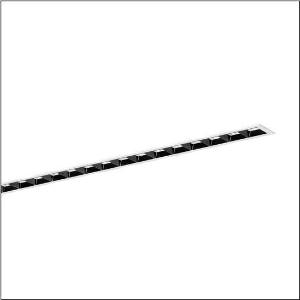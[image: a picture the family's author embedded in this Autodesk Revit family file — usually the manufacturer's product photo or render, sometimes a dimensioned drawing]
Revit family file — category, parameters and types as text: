
# Revit family: silica_21_51mx14dc4awb
name_source: partatom
category: Lighting Fixtures
units: mm (PartAtom-declared; Revit-internal decimal feet)

## family parameters
Cut with Voids When Loaded = No
Host = Face
Light Source = No
Part Type = Normal
Room Calculation Point = No
Round Connector Dimension = Use Diameter
Shared = No

## types (1)
- --- (1 x LED, 10800 lm, 73.7 W, 4000K)
    Apparent Load = 74 VA
    CIE Flux Codes = 74 94 99 100 100
    Color Rendering = 80
    Color Temperature = 4000K
    Default Elevation = 1800 mm
    Description = Silica 21, office luminaire, primary light control with darklight reflector, of PMMA, black, light emission: direct distribution, primary light characteristic: asymmetric, installation type: recessed, LED, rated luminous flux: 10.800lm, luminous efficacy: 147lm/W, light colour: 840, colour temperature: 4000K, control gear: DALI 2, with terminal, 3+2-pole, max. 2.5mm², mains connection: 220..240V, AC, 50/60Hz, rated input power: 73.7W, luminaire housing, of aluminium, traffic white (RAL 9016), length: 3.028mm, width: 79mm, height: 53mm, protection rating (complete): IP20, insulation class (complete): insulation class I (protective earthing), certification: CE, ENEC, VDE, permissible operating ambient temperature: 0..+35°C, standard: EN 50419, packaging unit: 1 piece
    Height = 0 mm  [stored 0 ft]
    Lamp = 1 x LED
    Lamp Light Flux = 10800 lm
    Lamp Power = 73.7 W
    Lamp count = 1
    Length = 3027 mm
    Luminous efficacy = 147 lm/W
    Manufacturer = Siteco
    ModVariant = No
    Model = 51MX14DC4AWB
    Mounting Place = Ceiling
    Mounting Type = Recessed
    Number of Poles = 1
    OnlyDefault = Yes
    Power Factor = 1
    Product Name = Silica 21
    Product group = office luminaire | ceiling recessed
    ProductGroupID = 400
    Protection Class = Protection class I
    Protection Degree = IP 20
    RLX_Detail_Level = 1
    RLX_Emergency_Light_Flux = 0 lm
    RLX_Emergency_Type = 0
    RLX_Emergency_Type_DB = No
    RlxData = <blob elided: 63217 chars, md5=e888084c>
    Socket = socket
    Standby Power = 0 W
    System Light Flux = 10800 lm
    System Power = 74 W
    Type Comments = factory setting: luminous flux: 100 % | dim-lin: 254 | 418 mA
    Type Image = l_1335880.jpg
    URL = http://relux.com
    VarID = @adj_124085
    Voltage = 0 V
    Weight = 0.00 kg
    Width = 79 mm

note: [stored X ft] marks values corroborated as IEEE doubles in the binary element streams (Revit-internal decimal feet)

## geometry (parser evidence)
native form markers: Blend x4, Sweep x11
no freeform markers — native parametric forms only
